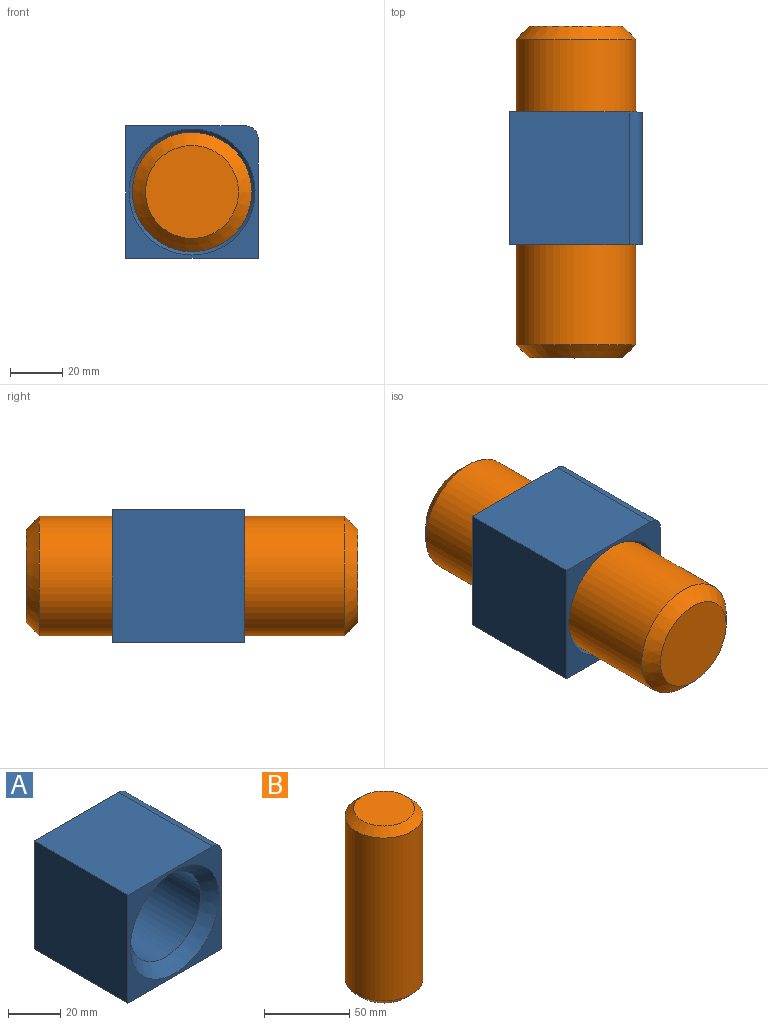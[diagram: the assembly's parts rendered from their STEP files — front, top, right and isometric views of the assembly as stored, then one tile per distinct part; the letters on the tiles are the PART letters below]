
ASSEMBLY  parts=2 mates=1
PART A: 9 faces, bbox 50.8x50.8x50.8 mm
  f0: plane 50.8x50.8mm, normal (-1,0,0), area 2580.6mm2, adj f1,f3,f4,f5
  f1: plane 50.8x50.8mm, normal (0,-1,0), area 745.9mm2, adj f0,f2,f4,f5,f7,f8
  f2: plane 50.8x45.72mm, normal (1,0,0), area 2322.6mm2, adj f1,f3,f5,f8
  f3: plane 50.8x50.8mm, normal (0,1,0), area 1435mm2, adj f0,f2,f4,f5,f6,f8
  f4: plane 50.8x45.72mm, normal (0,0,1), area 2322.6mm2, adj f0,f1,f3,f8
  f5: plane 50.8x50.8mm, normal (0,0,-1), area 2580.6mm2, adj f0,f1,f2,f3
  f6: cylinder r=19.05mm len=45.72mm, axis (0,-1,0), area 5472.4mm2, adj f3,f7
  f7: cone r=19.05mm half-angle=45deg, axis (0,-1,0), area 974.6mm2, adj f1,f6
  f8: cylinder r=5.08mm len=50.8mm, axis (0,-1,0), area 405.4mm2, adj f1,f2,f3,f4
PART B: 5 faces, bbox 45.7x45.7x127 mm
  f0: cylinder r=22.86mm len=116.84mm, axis (0,0,-1), area 16782.2mm2, adj f3,f4
  f1: plane 35.56x35.56mm, normal (0,0,1), area 993.1mm2, adj f3
  f2: plane 35.56x35.56mm, normal (0,0,-1), area 993.1mm2, adj f4
  f3: cone r=17.78mm half-angle=45deg, axis (0,0,-1), area 917.2mm2, adj f0,f1
  f4: cone r=22.86mm half-angle=45deg, axis (0,0,1), area 917.2mm2, adj f0,f2
PLACE A t=(66.89,43.28,13.82)mm
PLACE B rot(axis=(1,0,0),90deg) t=(142.38,127,-2.54)mm
MATE slider B.f0 <-> A.f6  axis (0,-1,0) through (92.29,5.08,39.22)mm
